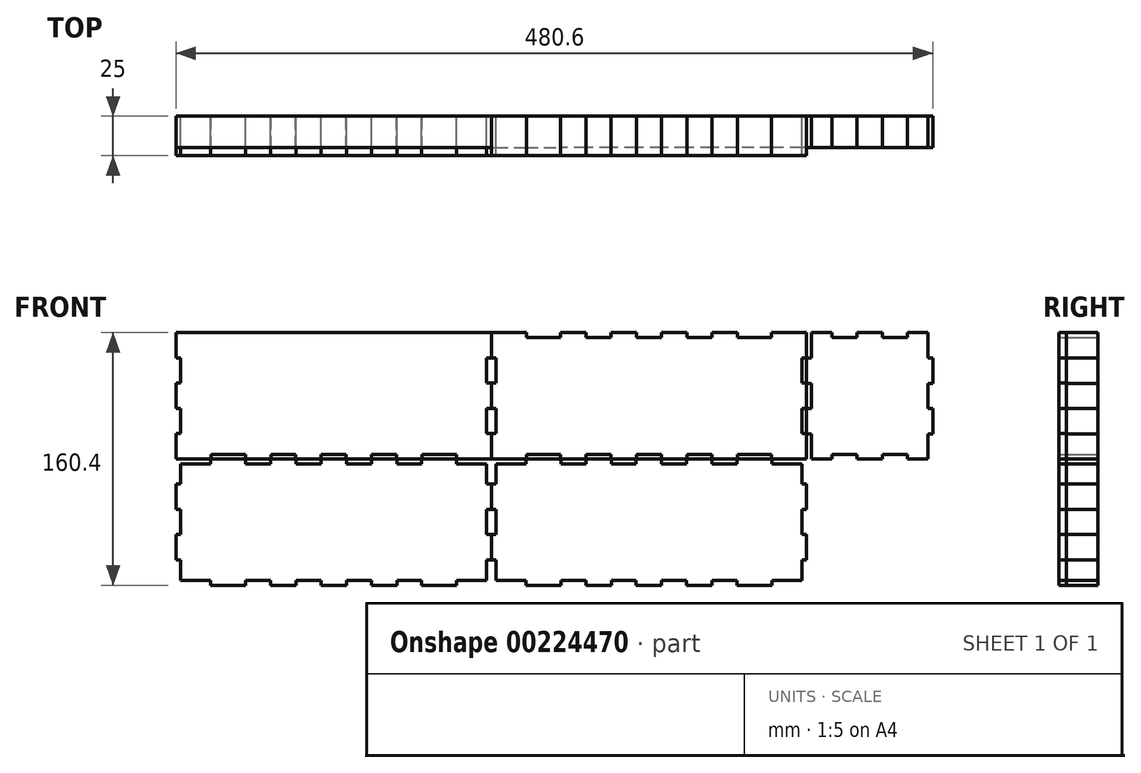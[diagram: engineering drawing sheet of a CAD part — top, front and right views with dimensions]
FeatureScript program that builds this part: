
annotation { "Feature Type Name" : "Feature", "Feature Type Description" : "" }
export const myFeature = defineFeature(function(context is Context, id is Id, definition is map)
    precondition{}
    {
        {
            var Q0;
            Q0=qCreatedBy(makeId("Front.planeOp"),FACE);
            var sketch = newSketch(context, id + "F0", { "sketchPlane" : qUnion([Q0])});
            skLineSegment(sketch, "E0", {"start": v(-240.3, 80.2) * mm, "end": v(-218.1, 80.2) * mm});
            skLineSegment(sketch, "E1", {"start": v(-218.1, 80.2) * mm, "end": v(-218.1, 77.2) * mm});
            skLineSegment(sketch, "E2", {"start": v(-218.1, 77.2) * mm, "end": v(-196.3, 77.2) * mm});
            skLineSegment(sketch, "E3", {"start": v(-196.3, 77.2) * mm, "end": v(-196.3, 80.2) * mm});
            skLineSegment(sketch, "E4", {"start": v(-196.3, 80.2) * mm, "end": v(-180.1, 80.2) * mm});
            skLineSegment(sketch, "E5", {"start": v(-180.1, 80.2) * mm, "end": v(-180.1, 77.2) * mm});
            skLineSegment(sketch, "E6", {"start": v(-180.1, 77.2) * mm, "end": v(-164.3, 77.2) * mm});
            skLineSegment(sketch, "E7", {"start": v(-164.3, 77.2) * mm, "end": v(-164.3, 80.2) * mm});
            skLineSegment(sketch, "E8", {"start": v(-164.3, 80.2) * mm, "end": v(-148.1, 80.2) * mm});
            skLineSegment(sketch, "E9", {"start": v(-148.1, 80.2) * mm, "end": v(-148.1, 77.2) * mm});
            skLineSegment(sketch, "E10", {"start": v(-148.1, 77.2) * mm, "end": v(-132.3, 77.2) * mm});
            skLineSegment(sketch, "E11", {"start": v(-132.3, 77.2) * mm, "end": v(-132.3, 80.2) * mm});
            skLineSegment(sketch, "E12", {"start": v(-132.3, 80.2) * mm, "end": v(-116.1, 80.2) * mm});
            skLineSegment(sketch, "E13", {"start": v(-116.1, 80.2) * mm, "end": v(-116.1, 77.2) * mm});
            skLineSegment(sketch, "E14", {"start": v(-116.1, 77.2) * mm, "end": v(-100.3, 77.2) * mm});
            skLineSegment(sketch, "E15", {"start": v(-100.3, 77.2) * mm, "end": v(-100.3, 80.2) * mm});
            skLineSegment(sketch, "E16", {"start": v(-100.3, 80.2) * mm, "end": v(-84.1, 80.2) * mm});
            skLineSegment(sketch, "E17", {"start": v(-84.1, 80.2) * mm, "end": v(-84.1, 77.2) * mm});
            skLineSegment(sketch, "E18", {"start": v(-84.1, 77.2) * mm, "end": v(-62.3, 77.2) * mm});
            skLineSegment(sketch, "E19", {"start": v(-62.3, 77.2) * mm, "end": v(-62.3, 80.2) * mm});
            skLineSegment(sketch, "E20", {"start": v(-62.3, 80.2) * mm, "end": v(-40.1, 80.2) * mm});
            skLineSegment(sketch, "E21", {"start": v(-40.1, 80.2) * mm, "end": v(-40.1, 64) * mm});
            skLineSegment(sketch, "E22", {"start": v(-40.1, 64) * mm, "end": v(-43.1, 64) * mm});
            skLineSegment(sketch, "E23", {"start": v(-43.1, 64) * mm, "end": v(-43.1, 48.2) * mm});
            skLineSegment(sketch, "E24", {"start": v(-43.1, 48.2) * mm, "end": v(-40.1, 48.2) * mm});
            skLineSegment(sketch, "E25", {"start": v(-40.1, 48.2) * mm, "end": v(-40.1, 32) * mm});
            skLineSegment(sketch, "E26", {"start": v(-40.1, 32) * mm, "end": v(-43.1, 32) * mm});
            skLineSegment(sketch, "E27", {"start": v(-43.1, 32) * mm, "end": v(-43.1, 16.2) * mm});
            skLineSegment(sketch, "E28", {"start": v(-43.1, 16.2) * mm, "end": v(-40.1, 16.2) * mm});
            skLineSegment(sketch, "E29", {"start": v(-40.1, 16.2) * mm, "end": v(-40.1, 0) * mm});
            skLineSegment(sketch, "E30", {"start": v(-40.1, 0) * mm, "end": v(-62.3, 0) * mm});
            skLineSegment(sketch, "E31", {"start": v(-62.3, 0) * mm, "end": v(-62.3, 3) * mm});
            skLineSegment(sketch, "E32", {"start": v(-62.3, 3) * mm, "end": v(-84.1, 3) * mm});
            skLineSegment(sketch, "E33", {"start": v(-84.1, 3) * mm, "end": v(-84.1, 0) * mm});
            skLineSegment(sketch, "E34", {"start": v(-84.1, 0) * mm, "end": v(-100.3, 0) * mm});
            skLineSegment(sketch, "E35", {"start": v(-100.3, 0) * mm, "end": v(-100.3, 3) * mm});
            skLineSegment(sketch, "E36", {"start": v(-100.3, 3) * mm, "end": v(-116.1, 3) * mm});
            skLineSegment(sketch, "E37", {"start": v(-116.1, 3) * mm, "end": v(-116.1, 0) * mm});
            skLineSegment(sketch, "E38", {"start": v(-116.1, 0) * mm, "end": v(-132.3, 0) * mm});
            skLineSegment(sketch, "E39", {"start": v(-132.3, 0) * mm, "end": v(-132.3, 3) * mm});
            skLineSegment(sketch, "E40", {"start": v(-132.3, 3) * mm, "end": v(-148.1, 3) * mm});
            skLineSegment(sketch, "E41", {"start": v(-148.1, 3) * mm, "end": v(-148.1, 0) * mm});
            skLineSegment(sketch, "E42", {"start": v(-148.1, 0) * mm, "end": v(-164.3, 0) * mm});
            skLineSegment(sketch, "E43", {"start": v(-164.3, 0) * mm, "end": v(-164.3, 3) * mm});
            skLineSegment(sketch, "E44", {"start": v(-164.3, 3) * mm, "end": v(-180.1, 3) * mm});
            skLineSegment(sketch, "E45", {"start": v(-180.1, 3) * mm, "end": v(-180.1, 0) * mm});
            skLineSegment(sketch, "E46", {"start": v(-180.1, 0) * mm, "end": v(-196.3, 0) * mm});
            skLineSegment(sketch, "E47", {"start": v(-196.3, 0) * mm, "end": v(-196.3, 3) * mm});
            skLineSegment(sketch, "E48", {"start": v(-196.3, 3) * mm, "end": v(-218.1, 3) * mm});
            skLineSegment(sketch, "E49", {"start": v(-218.1, 3) * mm, "end": v(-218.1, 0) * mm});
            skLineSegment(sketch, "E50", {"start": v(-218.1, 0) * mm, "end": v(-240.3, 0) * mm});
            skLineSegment(sketch, "E51", {"start": v(-240.3, 0) * mm, "end": v(-240.3, 16.2) * mm});
            skLineSegment(sketch, "E52", {"start": v(-240.3, 16.2) * mm, "end": v(-237.3, 16.2) * mm});
            skLineSegment(sketch, "E53", {"start": v(-237.3, 16.2) * mm, "end": v(-237.3, 32) * mm});
            skLineSegment(sketch, "E54", {"start": v(-237.3, 32) * mm, "end": v(-240.3, 32) * mm});
            skLineSegment(sketch, "E55", {"start": v(-240.3, 32) * mm, "end": v(-240.3, 48.2) * mm});
            skLineSegment(sketch, "E56", {"start": v(-240.3, 48.2) * mm, "end": v(-237.3, 48.2) * mm});
            skLineSegment(sketch, "E57", {"start": v(-237.3, 48.2) * mm, "end": v(-237.3, 64) * mm});
            skLineSegment(sketch, "E58", {"start": v(-237.3, 64) * mm, "end": v(-240.3, 64) * mm});
            skLineSegment(sketch, "E59", {"start": v(-240.3, 64) * mm, "end": v(-240.3, 80.2) * mm});
            skLineSegment(sketch, "E60", {"start": v(-40.1, 80.2) * mm, "end": v(-17.9, 80.2) * mm});
            skLineSegment(sketch, "E61", {"start": v(-17.9, 80.2) * mm, "end": v(-17.9, 77.2) * mm});
            skLineSegment(sketch, "E62", {"start": v(-17.9, 77.2) * mm, "end": v(3.9, 77.2) * mm});
            skLineSegment(sketch, "E63", {"start": v(3.9, 77.2) * mm, "end": v(3.9, 80.2) * mm});
            skLineSegment(sketch, "E64", {"start": v(3.9, 80.2) * mm, "end": v(20.1, 80.2) * mm});
            skLineSegment(sketch, "E65", {"start": v(20.1, 80.2) * mm, "end": v(20.1, 77.2) * mm});
            skLineSegment(sketch, "E66", {"start": v(20.1, 77.2) * mm, "end": v(35.9, 77.2) * mm});
            skLineSegment(sketch, "E67", {"start": v(35.9, 77.2) * mm, "end": v(35.9, 80.2) * mm});
            skLineSegment(sketch, "E68", {"start": v(35.9, 80.2) * mm, "end": v(52.1, 80.2) * mm});
            skLineSegment(sketch, "E69", {"start": v(52.1, 80.2) * mm, "end": v(52.1, 77.2) * mm});
            skLineSegment(sketch, "E70", {"start": v(52.1, 77.2) * mm, "end": v(67.9, 77.2) * mm});
            skLineSegment(sketch, "E71", {"start": v(67.9, 77.2) * mm, "end": v(67.9, 80.2) * mm});
            skLineSegment(sketch, "E72", {"start": v(67.9, 80.2) * mm, "end": v(84.1, 80.2) * mm});
            skLineSegment(sketch, "E73", {"start": v(84.1, 80.2) * mm, "end": v(84.1, 77.2) * mm});
            skLineSegment(sketch, "E74", {"start": v(84.1, 77.2) * mm, "end": v(99.9, 77.2) * mm});
            skLineSegment(sketch, "E75", {"start": v(99.9, 77.2) * mm, "end": v(99.9, 80.2) * mm});
            skLineSegment(sketch, "E76", {"start": v(99.9, 80.2) * mm, "end": v(116.1, 80.2) * mm});
            skLineSegment(sketch, "E77", {"start": v(116.1, 80.2) * mm, "end": v(116.1, 77.2) * mm});
            skLineSegment(sketch, "E78", {"start": v(116.1, 77.2) * mm, "end": v(137.9, 77.2) * mm});
            skLineSegment(sketch, "E79", {"start": v(137.9, 77.2) * mm, "end": v(137.9, 80.2) * mm});
            skLineSegment(sketch, "E80", {"start": v(137.9, 80.2) * mm, "end": v(160.1, 80.2) * mm});
            skLineSegment(sketch, "E81", {"start": v(160.1, 80.2) * mm, "end": v(160.1, 64) * mm});
            skLineSegment(sketch, "E82", {"start": v(160.1, 64) * mm, "end": v(157.1, 64) * mm});
            skLineSegment(sketch, "E83", {"start": v(157.1, 64) * mm, "end": v(157.1, 48.2) * mm});
            skLineSegment(sketch, "E84", {"start": v(157.1, 48.2) * mm, "end": v(160.1, 48.2) * mm});
            skLineSegment(sketch, "E85", {"start": v(160.1, 48.2) * mm, "end": v(160.1, 32) * mm});
            skLineSegment(sketch, "E86", {"start": v(160.1, 32) * mm, "end": v(157.1, 32) * mm});
            skLineSegment(sketch, "E87", {"start": v(157.1, 32) * mm, "end": v(157.1, 16.2) * mm});
            skLineSegment(sketch, "E88", {"start": v(157.1, 16.2) * mm, "end": v(160.1, 16.2) * mm});
            skLineSegment(sketch, "E89", {"start": v(160.1, 16.2) * mm, "end": v(160.1, 0) * mm});
            skLineSegment(sketch, "E90", {"start": v(160.1, 0) * mm, "end": v(137.9, 0) * mm});
            skLineSegment(sketch, "E91", {"start": v(137.9, 0) * mm, "end": v(137.9, 3) * mm});
            skLineSegment(sketch, "E92", {"start": v(137.9, 3) * mm, "end": v(116.1, 3) * mm});
            skLineSegment(sketch, "E93", {"start": v(116.1, 3) * mm, "end": v(116.1, 0) * mm});
            skLineSegment(sketch, "E94", {"start": v(116.1, 0) * mm, "end": v(99.9, 0) * mm});
            skLineSegment(sketch, "E95", {"start": v(99.9, 0) * mm, "end": v(99.9, 3) * mm});
            skLineSegment(sketch, "E96", {"start": v(99.9, 3) * mm, "end": v(84.1, 3) * mm});
            skLineSegment(sketch, "E97", {"start": v(84.1, 3) * mm, "end": v(84.1, 0) * mm});
            skLineSegment(sketch, "E98", {"start": v(84.1, 0) * mm, "end": v(67.9, 0) * mm});
            skLineSegment(sketch, "E99", {"start": v(67.9, 0) * mm, "end": v(67.9, 3) * mm});
            skLineSegment(sketch, "E100", {"start": v(67.9, 3) * mm, "end": v(52.1, 3) * mm});
            skLineSegment(sketch, "E101", {"start": v(52.1, 3) * mm, "end": v(52.1, 0) * mm});
            skLineSegment(sketch, "E102", {"start": v(52.1, 0) * mm, "end": v(35.9, 0) * mm});
            skLineSegment(sketch, "E103", {"start": v(35.9, 0) * mm, "end": v(35.9, 3) * mm});
            skLineSegment(sketch, "E104", {"start": v(35.9, 3) * mm, "end": v(20.1, 3) * mm});
            skLineSegment(sketch, "E105", {"start": v(20.1, 3) * mm, "end": v(20.1, 0) * mm});
            skLineSegment(sketch, "E106", {"start": v(20.1, 0) * mm, "end": v(3.9, 0) * mm});
            skLineSegment(sketch, "E107", {"start": v(3.9, 0) * mm, "end": v(3.9, 3) * mm});
            skLineSegment(sketch, "E108", {"start": v(3.9, 3) * mm, "end": v(-17.9, 3) * mm});
            skLineSegment(sketch, "E109", {"start": v(-17.9, 3) * mm, "end": v(-17.9, 0) * mm});
            skLineSegment(sketch, "E110", {"start": v(-17.9, 0) * mm, "end": v(-40.1, 0) * mm});
            skLineSegment(sketch, "E111", {"start": v(-40.1, 0) * mm, "end": v(-40.1, 16.2) * mm});
            skLineSegment(sketch, "E112", {"start": v(-40.1, 16.2) * mm, "end": v(-37.1, 16.2) * mm});
            skLineSegment(sketch, "E113", {"start": v(-37.1, 16.2) * mm, "end": v(-37.1, 32) * mm});
            skLineSegment(sketch, "E114", {"start": v(-37.1, 32) * mm, "end": v(-40.1, 32) * mm});
            skLineSegment(sketch, "E115", {"start": v(-40.1, 32) * mm, "end": v(-40.1, 48.2) * mm});
            skLineSegment(sketch, "E116", {"start": v(-40.1, 48.2) * mm, "end": v(-37.1, 48.2) * mm});
            skLineSegment(sketch, "E117", {"start": v(-37.1, 48.2) * mm, "end": v(-37.1, 64) * mm});
            skLineSegment(sketch, "E118", {"start": v(-37.1, 64) * mm, "end": v(-40.1, 64) * mm});
            skLineSegment(sketch, "E119", {"start": v(-40.1, 64) * mm, "end": v(-40.1, 80.2) * mm});
            skLineSegment(sketch, "E120", {"start": v(163.1, 80.2) * mm, "end": v(176.3, 80.2) * mm});
            skLineSegment(sketch, "E121", {"start": v(176.3, 80.2) * mm, "end": v(176.3, 77.2) * mm});
            skLineSegment(sketch, "E122", {"start": v(176.3, 77.2) * mm, "end": v(192.1, 77.2) * mm});
            skLineSegment(sketch, "E123", {"start": v(192.1, 77.2) * mm, "end": v(192.1, 80.2) * mm});
            skLineSegment(sketch, "E124", {"start": v(192.1, 80.2) * mm, "end": v(208.3, 80.2) * mm});
            skLineSegment(sketch, "E125", {"start": v(208.3, 80.2) * mm, "end": v(208.3, 77.2) * mm});
            skLineSegment(sketch, "E126", {"start": v(208.3, 77.2) * mm, "end": v(224.1, 77.2) * mm});
            skLineSegment(sketch, "E127", {"start": v(224.1, 77.2) * mm, "end": v(224.1, 80.2) * mm});
            skLineSegment(sketch, "E128", {"start": v(224.1, 80.2) * mm, "end": v(237.3, 80.2) * mm});
            skLineSegment(sketch, "E129", {"start": v(237.3, 80.2) * mm, "end": v(237.3, 64.2) * mm});
            skLineSegment(sketch, "E130", {"start": v(237.3, 64.2) * mm, "end": v(240.3, 64.2) * mm});
            skLineSegment(sketch, "E131", {"start": v(240.3, 64.2) * mm, "end": v(240.3, 48) * mm});
            skLineSegment(sketch, "E132", {"start": v(240.3, 48) * mm, "end": v(237.3, 48) * mm});
            skLineSegment(sketch, "E133", {"start": v(237.3, 48) * mm, "end": v(237.3, 32.2) * mm});
            skLineSegment(sketch, "E134", {"start": v(237.3, 32.2) * mm, "end": v(240.3, 32.2) * mm});
            skLineSegment(sketch, "E135", {"start": v(240.3, 32.2) * mm, "end": v(240.3, 16) * mm});
            skLineSegment(sketch, "E136", {"start": v(240.3, 16) * mm, "end": v(237.3, 16) * mm});
            skLineSegment(sketch, "E137", {"start": v(237.3, 16) * mm, "end": v(237.3, 0) * mm});
            skLineSegment(sketch, "E138", {"start": v(237.3, 0) * mm, "end": v(224.1, 0) * mm});
            skLineSegment(sketch, "E139", {"start": v(224.1, 0) * mm, "end": v(224.1, 3) * mm});
            skLineSegment(sketch, "E140", {"start": v(224.1, 3) * mm, "end": v(208.3, 3) * mm});
            skLineSegment(sketch, "E141", {"start": v(208.3, 3) * mm, "end": v(208.3, 0) * mm});
            skLineSegment(sketch, "E142", {"start": v(208.3, 0) * mm, "end": v(192.1, 0) * mm});
            skLineSegment(sketch, "E143", {"start": v(192.1, 0) * mm, "end": v(192.1, 3) * mm});
            skLineSegment(sketch, "E144", {"start": v(192.1, 3) * mm, "end": v(176.3, 3) * mm});
            skLineSegment(sketch, "E145", {"start": v(176.3, 3) * mm, "end": v(176.3, 0) * mm});
            skLineSegment(sketch, "E146", {"start": v(176.3, 0) * mm, "end": v(163.1, 0) * mm});
            skLineSegment(sketch, "E147", {"start": v(163.1, 0) * mm, "end": v(163.1, 16) * mm});
            skLineSegment(sketch, "E148", {"start": v(163.1, 16) * mm, "end": v(160.1, 16) * mm});
            skLineSegment(sketch, "E149", {"start": v(160.1, 16) * mm, "end": v(160.1, 32.2) * mm});
            skLineSegment(sketch, "E150", {"start": v(160.1, 32.2) * mm, "end": v(163.1, 32.2) * mm});
            skLineSegment(sketch, "E151", {"start": v(163.1, 32.2) * mm, "end": v(163.1, 48) * mm});
            skLineSegment(sketch, "E152", {"start": v(163.1, 48) * mm, "end": v(160.1, 48) * mm});
            skLineSegment(sketch, "E153", {"start": v(160.1, 48) * mm, "end": v(160.1, 64.2) * mm});
            skLineSegment(sketch, "E154", {"start": v(160.1, 64.2) * mm, "end": v(163.1, 64.2) * mm});
            skLineSegment(sketch, "E155", {"start": v(163.1, 64.2) * mm, "end": v(163.1, 80.2) * mm});
            skLineSegment(sketch, "E156", {"start": v(163.1, 0) * mm, "end": v(176.3, 0) * mm});
            skLineSegment(sketch, "E157", {"start": v(176.3, 0) * mm, "end": v(176.3, -3) * mm});
            skLineSegment(sketch, "E158", {"start": v(176.3, -3) * mm, "end": v(192.1, -3) * mm});
            skLineSegment(sketch, "E159", {"start": v(192.1, -3) * mm, "end": v(192.1, 0) * mm});
            skLineSegment(sketch, "E160", {"start": v(192.1, 0) * mm, "end": v(208.3, 0) * mm});
            skLineSegment(sketch, "E161", {"start": v(208.3, 0) * mm, "end": v(208.3, -3) * mm});
            skLineSegment(sketch, "E162", {"start": v(208.3, -3) * mm, "end": v(224.1, -3) * mm});
            skLineSegment(sketch, "E163", {"start": v(224.1, -3) * mm, "end": v(224.1, 0) * mm});
            skLineSegment(sketch, "E164", {"start": v(224.1, 0) * mm, "end": v(237.3, 0) * mm});
            skLineSegment(sketch, "E165", {"start": v(237.3, 0) * mm, "end": v(237.3, -16) * mm});
            skLineSegment(sketch, "E166", {"start": v(237.3, -16) * mm, "end": v(240.3, -16) * mm});
            skLineSegment(sketch, "E167", {"start": v(240.3, -16) * mm, "end": v(240.3, -32.2) * mm});
            skLineSegment(sketch, "E168", {"start": v(240.3, -32.2) * mm, "end": v(237.3, -32.2) * mm});
            skLineSegment(sketch, "E169", {"start": v(237.3, -32.2) * mm, "end": v(237.3, -48) * mm});
            skLineSegment(sketch, "E170", {"start": v(237.3, -48) * mm, "end": v(240.3, -48) * mm});
            skLineSegment(sketch, "E171", {"start": v(240.3, -48) * mm, "end": v(240.3, -64.2) * mm});
            skLineSegment(sketch, "E172", {"start": v(240.3, -64.2) * mm, "end": v(237.3, -64.2) * mm});
            skLineSegment(sketch, "E173", {"start": v(237.3, -64.2) * mm, "end": v(237.3, -80.2) * mm});
            skLineSegment(sketch, "E174", {"start": v(237.3, -80.2) * mm, "end": v(224.1, -80.2) * mm});
            skLineSegment(sketch, "E175", {"start": v(224.1, -80.2) * mm, "end": v(224.1, -77.2) * mm});
            skLineSegment(sketch, "E176", {"start": v(224.1, -77.2) * mm, "end": v(208.3, -77.2) * mm});
            skLineSegment(sketch, "E177", {"start": v(208.3, -77.2) * mm, "end": v(208.3, -80.2) * mm});
            skLineSegment(sketch, "E178", {"start": v(208.3, -80.2) * mm, "end": v(192.1, -80.2) * mm});
            skLineSegment(sketch, "E179", {"start": v(192.1, -80.2) * mm, "end": v(192.1, -77.2) * mm});
            skLineSegment(sketch, "E180", {"start": v(192.1, -77.2) * mm, "end": v(176.3, -77.2) * mm});
            skLineSegment(sketch, "E181", {"start": v(176.3, -77.2) * mm, "end": v(176.3, -80.2) * mm});
            skLineSegment(sketch, "E182", {"start": v(176.3, -80.2) * mm, "end": v(163.1, -80.2) * mm});
            skLineSegment(sketch, "E183", {"start": v(163.1, -80.2) * mm, "end": v(163.1, -64.2) * mm});
            skLineSegment(sketch, "E184", {"start": v(163.1, -64.2) * mm, "end": v(160.1, -64.2) * mm});
            skLineSegment(sketch, "E185", {"start": v(160.1, -64.2) * mm, "end": v(160.1, -48) * mm});
            skLineSegment(sketch, "E186", {"start": v(160.1, -48) * mm, "end": v(163.1, -48) * mm});
            skLineSegment(sketch, "E187", {"start": v(163.1, -48) * mm, "end": v(163.1, -32.2) * mm});
            skLineSegment(sketch, "E188", {"start": v(163.1, -32.2) * mm, "end": v(160.1, -32.2) * mm});
            skLineSegment(sketch, "E189", {"start": v(160.1, -32.2) * mm, "end": v(160.1, -16) * mm});
            skLineSegment(sketch, "E190", {"start": v(160.1, -16) * mm, "end": v(163.1, -16) * mm});
            skLineSegment(sketch, "E191", {"start": v(163.1, -16) * mm, "end": v(163.1, 0) * mm});
            skLineSegment(sketch, "E192", {"start": v(-237.3, -3) * mm, "end": v(-218.3, -3) * mm});
            skLineSegment(sketch, "E193", {"start": v(-218.3, -3) * mm, "end": v(-218.3, 0) * mm});
            skLineSegment(sketch, "E194", {"start": v(-218.3, 0) * mm, "end": v(-196.1, 0) * mm});
            skLineSegment(sketch, "E195", {"start": v(-196.1, 0) * mm, "end": v(-196.1, -3) * mm});
            skLineSegment(sketch, "E196", {"start": v(-196.1, -3) * mm, "end": v(-180.3, -3) * mm});
            skLineSegment(sketch, "E197", {"start": v(-180.3, -3) * mm, "end": v(-180.3, 0) * mm});
            skLineSegment(sketch, "E198", {"start": v(-180.3, 0) * mm, "end": v(-164.1, 0) * mm});
            skLineSegment(sketch, "E199", {"start": v(-164.1, 0) * mm, "end": v(-164.1, -3) * mm});
            skLineSegment(sketch, "E200", {"start": v(-164.1, -3) * mm, "end": v(-148.3, -3) * mm});
            skLineSegment(sketch, "E201", {"start": v(-148.3, -3) * mm, "end": v(-148.3, 0) * mm});
            skLineSegment(sketch, "E202", {"start": v(-148.3, 0) * mm, "end": v(-132.1, 0) * mm});
            skLineSegment(sketch, "E203", {"start": v(-132.1, 0) * mm, "end": v(-132.1, -3) * mm});
            skLineSegment(sketch, "E204", {"start": v(-132.1, -3) * mm, "end": v(-116.3, -3) * mm});
            skLineSegment(sketch, "E205", {"start": v(-116.3, -3) * mm, "end": v(-116.3, 0) * mm});
            skLineSegment(sketch, "E206", {"start": v(-116.3, 0) * mm, "end": v(-100.1, 0) * mm});
            skLineSegment(sketch, "E207", {"start": v(-100.1, 0) * mm, "end": v(-100.1, -3) * mm});
            skLineSegment(sketch, "E208", {"start": v(-100.1, -3) * mm, "end": v(-84.3, -3) * mm});
            skLineSegment(sketch, "E209", {"start": v(-84.3, -3) * mm, "end": v(-84.3, 0) * mm});
            skLineSegment(sketch, "E210", {"start": v(-84.3, 0) * mm, "end": v(-62.1, 0) * mm});
            skLineSegment(sketch, "E211", {"start": v(-62.1, 0) * mm, "end": v(-62.1, -3) * mm});
            skLineSegment(sketch, "E212", {"start": v(-62.1, -3) * mm, "end": v(-43.1, -3) * mm});
            skLineSegment(sketch, "E213", {"start": v(-43.1, -3) * mm, "end": v(-43.1, -16) * mm});
            skLineSegment(sketch, "E214", {"start": v(-43.1, -16) * mm, "end": v(-40.1, -16) * mm});
            skLineSegment(sketch, "E215", {"start": v(-40.1, -16) * mm, "end": v(-40.1, -32.2) * mm});
            skLineSegment(sketch, "E216", {"start": v(-40.1, -32.2) * mm, "end": v(-43.1, -32.2) * mm});
            skLineSegment(sketch, "E217", {"start": v(-43.1, -32.2) * mm, "end": v(-43.1, -48) * mm});
            skLineSegment(sketch, "E218", {"start": v(-43.1, -48) * mm, "end": v(-40.1, -48) * mm});
            skLineSegment(sketch, "E219", {"start": v(-40.1, -48) * mm, "end": v(-40.1, -64.2) * mm});
            skLineSegment(sketch, "E220", {"start": v(-40.1, -64.2) * mm, "end": v(-43.1, -64.2) * mm});
            skLineSegment(sketch, "E221", {"start": v(-43.1, -64.2) * mm, "end": v(-43.1, -77.2) * mm});
            skLineSegment(sketch, "E222", {"start": v(-43.1, -77.2) * mm, "end": v(-62.1, -77.2) * mm});
            skLineSegment(sketch, "E223", {"start": v(-62.1, -77.2) * mm, "end": v(-62.1, -80.2) * mm});
            skLineSegment(sketch, "E224", {"start": v(-62.1, -80.2) * mm, "end": v(-84.3, -80.2) * mm});
            skLineSegment(sketch, "E225", {"start": v(-84.3, -80.2) * mm, "end": v(-84.3, -77.2) * mm});
            skLineSegment(sketch, "E226", {"start": v(-84.3, -77.2) * mm, "end": v(-100.1, -77.2) * mm});
            skLineSegment(sketch, "E227", {"start": v(-100.1, -77.2) * mm, "end": v(-100.1, -80.2) * mm});
            skLineSegment(sketch, "E228", {"start": v(-100.1, -80.2) * mm, "end": v(-116.3, -80.2) * mm});
            skLineSegment(sketch, "E229", {"start": v(-116.3, -80.2) * mm, "end": v(-116.3, -77.2) * mm});
            skLineSegment(sketch, "E230", {"start": v(-116.3, -77.2) * mm, "end": v(-132.1, -77.2) * mm});
            skLineSegment(sketch, "E231", {"start": v(-132.1, -77.2) * mm, "end": v(-132.1, -80.2) * mm});
            skLineSegment(sketch, "E232", {"start": v(-132.1, -80.2) * mm, "end": v(-148.3, -80.2) * mm});
            skLineSegment(sketch, "E233", {"start": v(-148.3, -80.2) * mm, "end": v(-148.3, -77.2) * mm});
            skLineSegment(sketch, "E234", {"start": v(-148.3, -77.2) * mm, "end": v(-164.1, -77.2) * mm});
            skLineSegment(sketch, "E235", {"start": v(-164.1, -77.2) * mm, "end": v(-164.1, -80.2) * mm});
            skLineSegment(sketch, "E236", {"start": v(-164.1, -80.2) * mm, "end": v(-180.3, -80.2) * mm});
            skLineSegment(sketch, "E237", {"start": v(-180.3, -80.2) * mm, "end": v(-180.3, -77.2) * mm});
            skLineSegment(sketch, "E238", {"start": v(-180.3, -77.2) * mm, "end": v(-196.1, -77.2) * mm});
            skLineSegment(sketch, "E239", {"start": v(-196.1, -77.2) * mm, "end": v(-196.1, -80.2) * mm});
            skLineSegment(sketch, "E240", {"start": v(-196.1, -80.2) * mm, "end": v(-218.3, -80.2) * mm});
            skLineSegment(sketch, "E241", {"start": v(-218.3, -80.2) * mm, "end": v(-218.3, -77.2) * mm});
            skLineSegment(sketch, "E242", {"start": v(-218.3, -77.2) * mm, "end": v(-237.3, -77.2) * mm});
            skLineSegment(sketch, "E243", {"start": v(-237.3, -77.2) * mm, "end": v(-237.3, -64.2) * mm});
            skLineSegment(sketch, "E244", {"start": v(-237.3, -64.2) * mm, "end": v(-240.3, -64.2) * mm});
            skLineSegment(sketch, "E245", {"start": v(-240.3, -64.2) * mm, "end": v(-240.3, -48) * mm});
            skLineSegment(sketch, "E246", {"start": v(-240.3, -48) * mm, "end": v(-237.3, -48) * mm});
            skLineSegment(sketch, "E247", {"start": v(-237.3, -48) * mm, "end": v(-237.3, -32.2) * mm});
            skLineSegment(sketch, "E248", {"start": v(-237.3, -32.2) * mm, "end": v(-240.3, -32.2) * mm});
            skLineSegment(sketch, "E249", {"start": v(-240.3, -32.2) * mm, "end": v(-240.3, -16) * mm});
            skLineSegment(sketch, "E250", {"start": v(-240.3, -16) * mm, "end": v(-237.3, -16) * mm});
            skLineSegment(sketch, "E251", {"start": v(-237.3, -16) * mm, "end": v(-237.3, -3) * mm});
            skLineSegment(sketch, "E252", {"start": v(-37.1, -3) * mm, "end": v(-18.1, -3) * mm});
            skLineSegment(sketch, "E253", {"start": v(-18.1, -3) * mm, "end": v(-18.1, 0) * mm});
            skLineSegment(sketch, "E254", {"start": v(-18.1, 0) * mm, "end": v(4.1, 0) * mm});
            skLineSegment(sketch, "E255", {"start": v(4.1, 0) * mm, "end": v(4.1, -3) * mm});
            skLineSegment(sketch, "E256", {"start": v(4.1, -3) * mm, "end": v(19.9, -3) * mm});
            skLineSegment(sketch, "E257", {"start": v(19.9, -3) * mm, "end": v(19.9, 0) * mm});
            skLineSegment(sketch, "E258", {"start": v(19.9, 0) * mm, "end": v(36.1, 0) * mm});
            skLineSegment(sketch, "E259", {"start": v(36.1, 0) * mm, "end": v(36.1, -3) * mm});
            skLineSegment(sketch, "E260", {"start": v(36.1, -3) * mm, "end": v(51.9, -3) * mm});
            skLineSegment(sketch, "E261", {"start": v(51.9, -3) * mm, "end": v(51.9, 0) * mm});
            skLineSegment(sketch, "E262", {"start": v(51.9, 0) * mm, "end": v(68.1, 0) * mm});
            skLineSegment(sketch, "E263", {"start": v(68.1, 0) * mm, "end": v(68.1, -3) * mm});
            skLineSegment(sketch, "E264", {"start": v(68.1, -3) * mm, "end": v(83.9, -3) * mm});
            skLineSegment(sketch, "E265", {"start": v(83.9, -3) * mm, "end": v(83.9, 0) * mm});
            skLineSegment(sketch, "E266", {"start": v(83.9, 0) * mm, "end": v(100.1, 0) * mm});
            skLineSegment(sketch, "E267", {"start": v(100.1, 0) * mm, "end": v(100.1, -3) * mm});
            skLineSegment(sketch, "E268", {"start": v(100.1, -3) * mm, "end": v(115.9, -3) * mm});
            skLineSegment(sketch, "E269", {"start": v(115.9, -3) * mm, "end": v(115.9, 0) * mm});
            skLineSegment(sketch, "E270", {"start": v(115.9, 0) * mm, "end": v(138.1, 0) * mm});
            skLineSegment(sketch, "E271", {"start": v(138.1, 0) * mm, "end": v(138.1, -3) * mm});
            skLineSegment(sketch, "E272", {"start": v(138.1, -3) * mm, "end": v(157.1, -3) * mm});
            skLineSegment(sketch, "E273", {"start": v(157.1, -3) * mm, "end": v(157.1, -16) * mm});
            skLineSegment(sketch, "E274", {"start": v(157.1, -16) * mm, "end": v(160.1, -16) * mm});
            skLineSegment(sketch, "E275", {"start": v(160.1, -16) * mm, "end": v(160.1, -32.2) * mm});
            skLineSegment(sketch, "E276", {"start": v(160.1, -32.2) * mm, "end": v(157.1, -32.2) * mm});
            skLineSegment(sketch, "E277", {"start": v(157.1, -32.2) * mm, "end": v(157.1, -48) * mm});
            skLineSegment(sketch, "E278", {"start": v(157.1, -48) * mm, "end": v(160.1, -48) * mm});
            skLineSegment(sketch, "E279", {"start": v(160.1, -48) * mm, "end": v(160.1, -64.2) * mm});
            skLineSegment(sketch, "E280", {"start": v(160.1, -64.2) * mm, "end": v(157.1, -64.2) * mm});
            skLineSegment(sketch, "E281", {"start": v(157.1, -64.2) * mm, "end": v(157.1, -77.2) * mm});
            skLineSegment(sketch, "E282", {"start": v(157.1, -77.2) * mm, "end": v(138.1, -77.2) * mm});
            skLineSegment(sketch, "E283", {"start": v(138.1, -77.2) * mm, "end": v(138.1, -80.2) * mm});
            skLineSegment(sketch, "E284", {"start": v(138.1, -80.2) * mm, "end": v(115.9, -80.2) * mm});
            skLineSegment(sketch, "E285", {"start": v(115.9, -80.2) * mm, "end": v(115.9, -77.2) * mm});
            skLineSegment(sketch, "E286", {"start": v(115.9, -77.2) * mm, "end": v(100.1, -77.2) * mm});
            skLineSegment(sketch, "E287", {"start": v(100.1, -77.2) * mm, "end": v(100.1, -80.2) * mm});
            skLineSegment(sketch, "E288", {"start": v(100.1, -80.2) * mm, "end": v(83.9, -80.2) * mm});
            skLineSegment(sketch, "E289", {"start": v(83.9, -80.2) * mm, "end": v(83.9, -77.2) * mm});
            skLineSegment(sketch, "E290", {"start": v(83.9, -77.2) * mm, "end": v(68.1, -77.2) * mm});
            skLineSegment(sketch, "E291", {"start": v(68.1, -77.2) * mm, "end": v(68.1, -80.2) * mm});
            skLineSegment(sketch, "E292", {"start": v(68.1, -80.2) * mm, "end": v(51.9, -80.2) * mm});
            skLineSegment(sketch, "E293", {"start": v(51.9, -80.2) * mm, "end": v(51.9, -77.2) * mm});
            skLineSegment(sketch, "E294", {"start": v(51.9, -77.2) * mm, "end": v(36.1, -77.2) * mm});
            skLineSegment(sketch, "E295", {"start": v(36.1, -77.2) * mm, "end": v(36.1, -80.2) * mm});
            skLineSegment(sketch, "E296", {"start": v(36.1, -80.2) * mm, "end": v(19.9, -80.2) * mm});
            skLineSegment(sketch, "E297", {"start": v(19.9, -80.2) * mm, "end": v(19.9, -77.2) * mm});
            skLineSegment(sketch, "E298", {"start": v(19.9, -77.2) * mm, "end": v(4.1, -77.2) * mm});
            skLineSegment(sketch, "E299", {"start": v(4.1, -77.2) * mm, "end": v(4.1, -80.2) * mm});
            skLineSegment(sketch, "E300", {"start": v(4.1, -80.2) * mm, "end": v(-18.1, -80.2) * mm});
            skLineSegment(sketch, "E301", {"start": v(-18.1, -80.2) * mm, "end": v(-18.1, -77.2) * mm});
            skLineSegment(sketch, "E302", {"start": v(-18.1, -77.2) * mm, "end": v(-37.1, -77.2) * mm});
            skLineSegment(sketch, "E303", {"start": v(-37.1, -77.2) * mm, "end": v(-37.1, -64.2) * mm});
            skLineSegment(sketch, "E304", {"start": v(-37.1, -64.2) * mm, "end": v(-40.1, -64.2) * mm});
            skLineSegment(sketch, "E305", {"start": v(-40.1, -64.2) * mm, "end": v(-40.1, -48) * mm});
            skLineSegment(sketch, "E306", {"start": v(-40.1, -48) * mm, "end": v(-37.1, -48) * mm});
            skLineSegment(sketch, "E307", {"start": v(-37.1, -48) * mm, "end": v(-37.1, -32.2) * mm});
            skLineSegment(sketch, "E308", {"start": v(-37.1, -32.2) * mm, "end": v(-40.1, -32.2) * mm});
            skLineSegment(sketch, "E309", {"start": v(-40.1, -32.2) * mm, "end": v(-40.1, -16) * mm});
            skLineSegment(sketch, "E310", {"start": v(-40.1, -16) * mm, "end": v(-37.1, -16) * mm});
            skLineSegment(sketch, "E311", {"start": v(-37.1, -16) * mm, "end": v(-37.1, -3) * mm});
            skSolve(sketch);
        }
        {
            var Q0;
            Q0=makeQuery(id+"F0.imprint","IMPRINT",FACE,{"disambiguationData":[TD([[makeQuery(id+"F0.imprint","IMPRINT",EDGE,{"derivedFrom":sQuery(id+"F0.wireOp",EDGE,"E156")}),-1.0]])]});
            var Q1;
            Q1=makeQuery(id+"F0.imprint","IMPRINT",FACE,{"disambiguationData":[TD([[makeQuery(id+"F0.imprint","IMPRINT",EDGE,{"derivedFrom":sQuery(id+"F0.wireOp",EDGE,"E192")}),-1.0]])]});
            var Q2;
            Q2=makeQuery(id+"F0.imprint","IMPRINT",FACE,{"disambiguationData":[TD([[makeQuery(id+"F0.imprint","IMPRINT",EDGE,{"derivedFrom":sQuery(id+"F0.wireOp",EDGE,"E60")}),-1.0]])]});
            extrude(context, id + "F1", {"entities" : qUnion([Q0, Q1, Q2]), "depth" : 25 * mm});
        }
        {
            var Q0;
            Q0=makeQuery(id+"F0.imprint","IMPRINT",FACE,{"disambiguationData":[TD([[makeQuery(id+"F0.imprint","IMPRINT",EDGE,{"derivedFrom":sQuery(id+"F0.wireOp",EDGE,"E0")}),-1.0]])]});
            var Q1;
            Q1=makeQuery(id+"F0.imprint","IMPRINT",FACE,{"disambiguationData":[TD([[makeQuery(id+"F0.imprint","IMPRINT",EDGE,{"derivedFrom":sQuery(id+"F0.wireOp",EDGE,"E252")}),-1.0]])]});
            var Q2;
            Q2=makeQuery(id+"F0.imprint","IMPRINT",FACE,{"disambiguationData":[TD([[makeQuery(id+"F0.imprint","IMPRINT",EDGE,{"derivedFrom":sQuery(id+"F0.wireOp",EDGE,"E120")}),-1.0]])]});
            extrude(context, id + "F2", {"entities" : qUnion([Q0, Q1, Q2]), "depth" : 20 * mm});
        }
        {
            var Q0;
            Q0=makeQuery(id+"F2.opExtrude","CAP_FACE",FACE,{"disambiguationData":[OSD([sQuery(id+"F0.wireOp",EDGE,"E0"),sQuery(id+"F0.wireOp",EDGE,"E1"),sQuery(id+"F0.wireOp",EDGE,"E2"),sQuery(id+"F0.wireOp",EDGE,"E3"),sQuery(id+"F0.wireOp",EDGE,"E4"),sQuery(id+"F0.wireOp",EDGE,"E5"),sQuery(id+"F0.wireOp",EDGE,"E6"),sQuery(id+"F0.wireOp",EDGE,"E7"),sQuery(id+"F0.wireOp",EDGE,"E8"),sQuery(id+"F0.wireOp",EDGE,"E9"),sQuery(id+"F0.wireOp",EDGE,"E10"),sQuery(id+"F0.wireOp",EDGE,"E11"),sQuery(id+"F0.wireOp",EDGE,"E12"),sQuery(id+"F0.wireOp",EDGE,"E13"),sQuery(id+"F0.wireOp",EDGE,"E14"),sQuery(id+"F0.wireOp",EDGE,"E15"),sQuery(id+"F0.wireOp",EDGE,"E16"),sQuery(id+"F0.wireOp",EDGE,"E17"),sQuery(id+"F0.wireOp",EDGE,"E18"),sQuery(id+"F0.wireOp",EDGE,"E19"),sQuery(id+"F0.wireOp",EDGE,"E20"),sQuery(id+"F0.wireOp",EDGE,"E22"),sQuery(id+"F0.wireOp",EDGE,"E23"),sQuery(id+"F0.wireOp",EDGE,"E24"),sQuery(id+"F0.wireOp",EDGE,"E26"),sQuery(id+"F0.wireOp",EDGE,"E27"),sQuery(id+"F0.wireOp",EDGE,"E28"),sQuery(id+"F0.wireOp",EDGE,"E30"),sQuery(id+"F0.wireOp",EDGE,"E31"),sQuery(id+"F0.wireOp",EDGE,"E32"),sQuery(id+"F0.wireOp",EDGE,"E33"),sQuery(id+"F0.wireOp",EDGE,"E34"),sQuery(id+"F0.wireOp",EDGE,"E35"),sQuery(id+"F0.wireOp",EDGE,"E36"),sQuery(id+"F0.wireOp",EDGE,"E37"),sQuery(id+"F0.wireOp",EDGE,"E38"),sQuery(id+"F0.wireOp",EDGE,"E39"),sQuery(id+"F0.wireOp",EDGE,"E40"),sQuery(id+"F0.wireOp",EDGE,"E41"),sQuery(id+"F0.wireOp",EDGE,"E42"),sQuery(id+"F0.wireOp",EDGE,"E43"),sQuery(id+"F0.wireOp",EDGE,"E44"),sQuery(id+"F0.wireOp",EDGE,"E45"),sQuery(id+"F0.wireOp",EDGE,"E46"),sQuery(id+"F0.wireOp",EDGE,"E47"),sQuery(id+"F0.wireOp",EDGE,"E48"),sQuery(id+"F0.wireOp",EDGE,"E49"),sQuery(id+"F0.wireOp",EDGE,"E50"),sQuery(id+"F0.wireOp",EDGE,"E51"),sQuery(id+"F0.wireOp",EDGE,"E52"),sQuery(id+"F0.wireOp",EDGE,"E53"),sQuery(id+"F0.wireOp",EDGE,"E54"),sQuery(id+"F0.wireOp",EDGE,"E55"),sQuery(id+"F0.wireOp",EDGE,"E56"),sQuery(id+"F0.wireOp",EDGE,"E57"),sQuery(id+"F0.wireOp",EDGE,"E58"),sQuery(id+"F0.wireOp",EDGE,"E59"),sQuery(id+"F0.wireOp",EDGE,"E111"),sQuery(id+"F0.wireOp",EDGE,"E115"),sQuery(id+"F0.wireOp",EDGE,"E119"),sQuery(id+"F0.wireOp",EDGE,"E194"),sQuery(id+"F0.wireOp",EDGE,"E198"),sQuery(id+"F0.wireOp",EDGE,"E202"),sQuery(id+"F0.wireOp",EDGE,"E206"),sQuery(id+"F0.wireOp",EDGE,"E210")])],"isStart":false});
            var sketch = newSketch(context, id + "F3", { "sketchPlane" : qUnion([Q0])});
            skLineSegment(sketch, "E312.bottom", {"start": v(-218.1, 80.2) * mm, "end": v(-62.3, 80.2) * mm});
            skLineSegment(sketch, "E312.top", {"start": v(-218.1, 77.2) * mm, "end": v(-62.3, 77.2) * mm});
            skLineSegment(sketch, "E312.left", {"start": v(-218.1, 80.2) * mm, "end": v(-218.1, 77.2) * mm});
            skLineSegment(sketch, "E312.right", {"start": v(-62.3, 80.2) * mm, "end": v(-62.3, 77.2) * mm});
            skSolve(sketch);
        }
        {
            var Q0;
            Q0=qSketchRegion(id+"F3",true);
            extrude(context, id + "F4", {"entities" : qUnion([Q0]), "operationType" : NewBodyOperationType.ADD, "oppositeDirection" : true, "depth" : 20 * mm});
        }
    });
